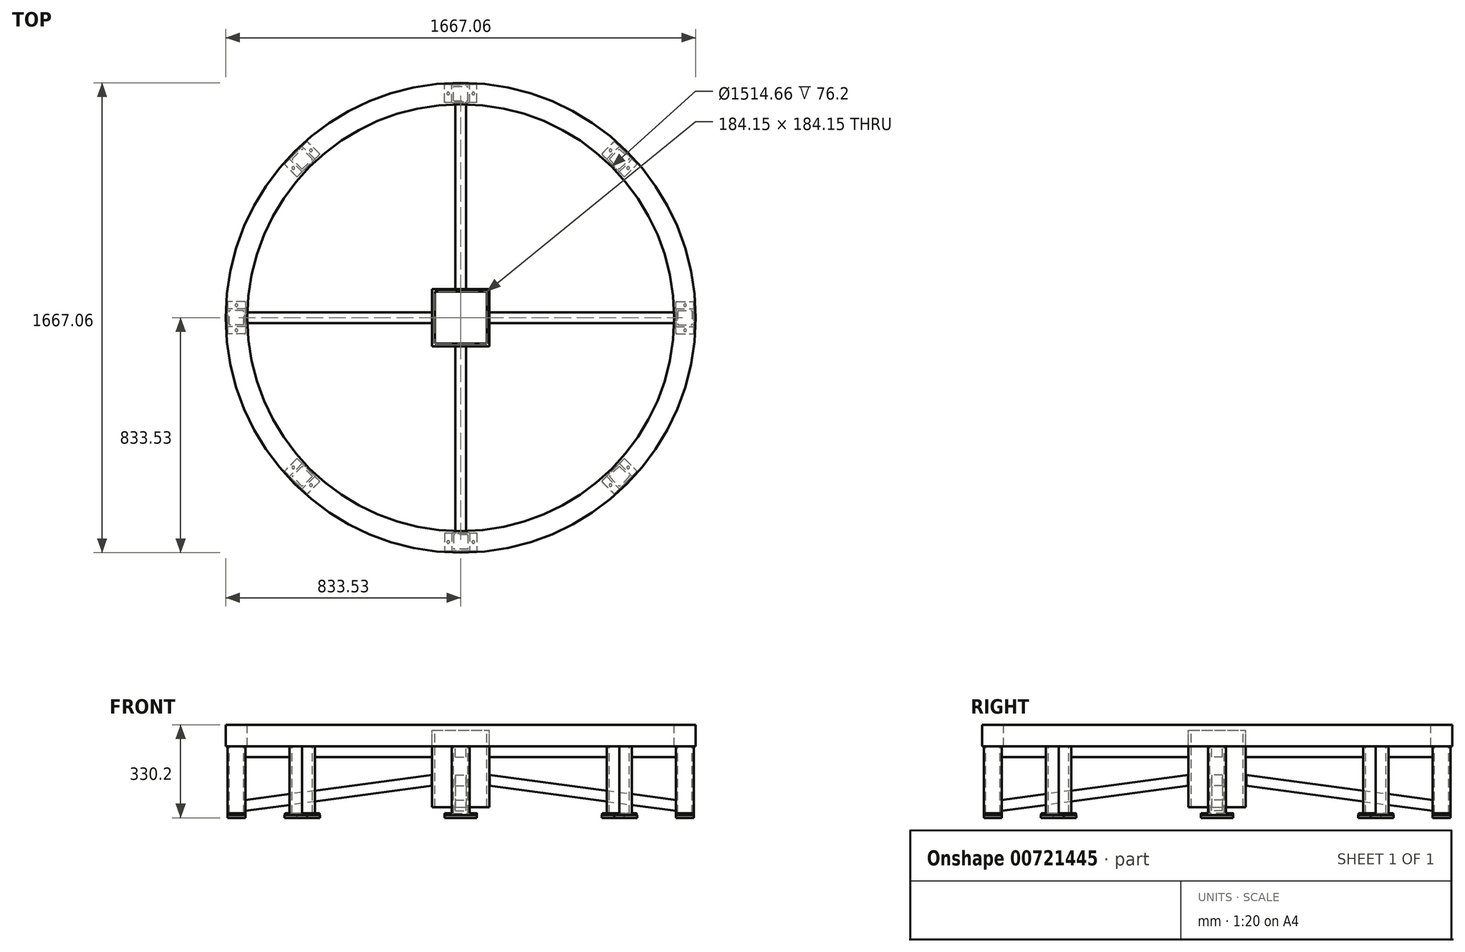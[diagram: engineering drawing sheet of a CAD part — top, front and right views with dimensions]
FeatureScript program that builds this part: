
annotation { "Feature Type Name" : "Feature", "Feature Type Description" : "" }
export const myFeature = defineFeature(function(context is Context, id is Id, definition is map)
    precondition{}
    {
        {
            var Q0;
            Q0=qCreatedBy(makeId("Front.planeOp"),FACE);
            var sketch = newSketch(context, id + "F0", { "sketchPlane" : qUnion([Q0])});
            skLineSegment(sketch, "E0.bottom", {"start": v(757.33, 0) * mm, "end": v(833.53, 0) * mm});
            skLineSegment(sketch, "E0.top", {"start": v(757.33, -76.2) * mm, "end": v(833.53, -76.2) * mm});
            skLineSegment(sketch, "E0.left", {"start": v(757.33, 0) * mm, "end": v(757.33, -76.2) * mm});
            skLineSegment(sketch, "E0.right", {"start": v(833.53, 0) * mm, "end": v(833.53, -76.2) * mm});
            skLineSegment(sketch, "E1.0", {"start": v(763.68, -69.85) * mm, "end": v(827.18, -69.85) * mm});
            skLineSegment(sketch, "E2.0", {"start": v(763.68, -6.35) * mm, "end": v(763.68, -69.85) * mm});
            skLineSegment(sketch, "E3.0", {"start": v(763.68, -6.35) * mm, "end": v(827.18, -6.35) * mm});
            skLineSegment(sketch, "E4.0", {"start": v(827.18, -6.35) * mm, "end": v(827.18, -69.85) * mm});
            skLineSegment(sketch, "E5", {"start": v(0, 0) * mm, "end": v(0, -46.56) * mm, "construction": true});
            skSolve(sketch);
        }
        {
            var Q0;
            Q0=makeQuery(id+"F0.imprint","IMPRINT",FACE,{"disambiguationData":[TD([[makeQuery(id+"F0.imprint","IMPRINT",EDGE,{"derivedFrom":sQuery(id+"F0.wireOp",EDGE,"E0.bottom")}),-1.0]])]});
            var Q1;
            Q1=makeQuery(id+"F0.imprint","IMPRINT",FACE,{"disambiguationData":[TD([[makeQuery(id+"F0.imprint","IMPRINT",EDGE,{"derivedFrom":sQuery(id+"F0.wireOp",EDGE,"E1.0")}),1.0]])]});
            var Q2;
            Q2=sQuery(id+"F0.wireOp",EDGE,"E0.bottom");
            var Q3;
            Q3=sQuery(id+"F0.wireOp",EDGE,"E3.0");
            var Q4;
            Q4=sQuery(id+"F0.wireOp",EDGE,"E0.left");
            var Q5;
            Q5=sQuery(id+"F0.wireOp",EDGE,"E1.0");
            var Q6;
            Q6=sQuery(id+"F0.wireOp",EDGE,"E0.top");
            var Q7;
            Q7=sQuery(id+"F0.wireOp",EDGE,"E4.0");
            var Q8;
            Q8=sQuery(id+"F0.wireOp",EDGE,"E0.right");
            var Q9;
            Q9=sQuery(id+"F0.wireOp",EDGE,"E2.0");
            var Q10;
            Q10=sQuery(id+"F0.wireOp",EDGE,"E5");
            revolve(context, id + "F1", {"surfaceOperationType" : NewSurfaceOperationType.NEW, "entities" : qUnion([Q0, Q1]), "surfaceEntities" : qUnion([Q2, Q3, Q4, Q5, Q6, Q7, Q8, Q9]), "axis" : qUnion([Q10]), "revolveType" : RevolveType.FULL});
        }
        {
            var Q0;
            Q0=qCreatedBy(makeId("Top.planeOp"),FACE);
            cPlane(context, id + "F2", {"entities" : qUnion([Q0]), "cplaneType" : CPlaneType.OFFSET, "offset" : 76.2 * mm, "oppositeDirection" : true, "width" : 152.4 * mm, "height" : 152.4 * mm});
        }
        {
            var Q0;
            Q0=qCreatedBy(id+"F2.planeOp",FACE);
            var sketch = newSketch(context, id + "F3", { "sketchPlane" : qUnion([Q0])});
            skLineSegment(sketch, "E6.bottom", {"start": v(-31.75, 763.68) * mm, "end": v(31.75, 763.68) * mm});
            skLineSegment(sketch, "E6.top", {"start": v(-31.75, 827.18) * mm, "end": v(31.75, 827.18) * mm});
            skLineSegment(sketch, "E6.left", {"start": v(-31.75, 763.68) * mm, "end": v(-31.75, 827.18) * mm});
            skLineSegment(sketch, "E6.right", {"start": v(31.75, 763.68) * mm, "end": v(31.75, 827.18) * mm});
            skLineSegment(sketch, "E7.0", {"start": v(-25.4, 770.03) * mm, "end": v(25.4, 770.03) * mm});
            skLineSegment(sketch, "E8.0", {"start": v(-25.4, 770.03) * mm, "end": v(-25.4, 820.83) * mm});
            skLineSegment(sketch, "E9.0", {"start": v(-25.4, 820.83) * mm, "end": v(25.4, 820.83) * mm});
            skLineSegment(sketch, "E10.0", {"start": v(25.4, 770.03) * mm, "end": v(25.4, 820.83) * mm});
            skSolve(sketch);
        }
        {
            var Q0;
            Q0=qSketchRegion(id+"F3",true);
            extrude(context, id + "F4", {"entities" : qUnion([Q0]), "oppositeDirection" : true, "depth" : 238.12 * mm, "offsetDistance" : 25.4 * mm});
        }
        {
            var Q0;
            Q0=makeQuery(id+"F4.opExtrude","CAP_FACE",FACE,{"disambiguationData":[OSD([sQuery(id+"F3.wireOp",EDGE,"E6.bottom"),sQuery(id+"F3.wireOp",EDGE,"E6.top"),sQuery(id+"F3.wireOp",EDGE,"E6.left"),sQuery(id+"F3.wireOp",EDGE,"E6.right"),sQuery(id+"F3.wireOp",EDGE,"E7.0"),sQuery(id+"F3.wireOp",EDGE,"E8.0"),sQuery(id+"F3.wireOp",EDGE,"E9.0"),sQuery(id+"F3.wireOp",EDGE,"E10.0")])],"isStart":false});
            var sketch = newSketch(context, id + "F5", { "sketchPlane" : qUnion([Q0])});
            skLineSegment(sketch, "E11.bottom", {"start": v(57.15, -763.68) * mm, "end": v(-57.15, -763.68) * mm});
            skLineSegment(sketch, "E11.top", {"start": v(57.15, -827.18) * mm, "end": v(-57.15, -827.18) * mm});
            skLineSegment(sketch, "E11.left", {"start": v(57.15, -763.68) * mm, "end": v(57.15, -827.18) * mm});
            skLineSegment(sketch, "E11.right", {"start": v(-57.15, -763.68) * mm, "end": v(-57.15, -827.18) * mm});
            skCircle(sketch, "E12", {"center": v(44.45, -795.43) * mm, "radius": 4.76 * mm});
            skCircle(sketch, "E13.1.0.0", {"center": v(-44.45, -795.43) * mm, "radius": 4.76 * mm});
            skLineSegment(sketch, "E13.direction1", {"start": v(44.45, -795.43) * mm, "end": v(-44.45, -795.43) * mm, "construction": true});
            skSolve(sketch);
        }
        {
            var Q0;
            Q0 = qSketchRegion(id + "F5", true);
            extrude(context, id + "F6", {"entities" : qUnion([Q0]), "operationType" : NewBodyOperationType.ADD, "depth" : 6.35 * mm, "offsetDistance" : 25.4 * mm});
        }
        {
            var Q0;
            Q0=makeQuery(id+"F6.opExtrude","SWEPT_EDGE",EDGE,{"disambiguationData":[OSD([sQuery(id+"F5.wireOp",EDGE,"E11.top"),sQuery(id+"F5.wireOp",EDGE,"E11.left")])]});
            var Q1;
            Q1=makeQuery(id+"F6.opExtrude","SWEPT_EDGE",EDGE,{"disambiguationData":[OSD([sQuery(id+"F5.wireOp",EDGE,"E11.bottom"),sQuery(id+"F5.wireOp",EDGE,"E11.left")])]});
            var Q2;
            Q2=makeQuery(id+"F6.opExtrude","SWEPT_EDGE",EDGE,{"disambiguationData":[OSD([sQuery(id+"F5.wireOp",EDGE,"E11.top"),sQuery(id+"F5.wireOp",EDGE,"E11.right")])]});
            var Q3;
            Q3=makeQuery(id+"F6.opExtrude","SWEPT_EDGE",EDGE,{"disambiguationData":[OSD([sQuery(id+"F5.wireOp",EDGE,"E11.bottom"),sQuery(id+"F5.wireOp",EDGE,"E11.right")])]});
            fillet(context, id + "F7", {"entities" : qUnion([Q0, Q1, Q2, Q3]), "radius" : 3.17 * mm, "tangentPropagation" : true, "allowEdgeOverflow" : false});
        }
        {
            var Q0;
            Q0=makeQuery(id+"F6.opExtrude","CAP_FACE",FACE,{"disambiguationData":[OSD([sQuery(id+"F5.wireOp",EDGE,"E11.bottom"),sQuery(id+"F5.wireOp",EDGE,"E11.top"),sQuery(id+"F5.wireOp",EDGE,"E11.left"),sQuery(id+"F5.wireOp",EDGE,"E11.right"),sQuery(id+"F5.wireOp",EDGE,"E12"),sQuery(id+"F5.wireOp",EDGE,"E13.1.0.0")])],"isStart":false});
            var sketch = newSketch(context, id + "F8", { "sketchPlane" : qUnion([Q0])});
            skLineSegment(sketch, "E14.bottom", {"start": v(57.15, -763.68) * mm, "end": v(-57.15, -763.68) * mm});
            skLineSegment(sketch, "E14.top", {"start": v(57.15, -827.18) * mm, "end": v(-57.15, -827.18) * mm});
            skLineSegment(sketch, "E14.left", {"start": v(57.15, -763.68) * mm, "end": v(57.15, -827.18) * mm});
            skLineSegment(sketch, "E14.right", {"start": v(-57.15, -763.68) * mm, "end": v(-57.15, -827.18) * mm});
            skSolve(sketch);
        }
        {
            var Q0;
            Q0 = qSketchRegion(id + "F8", true);
            extrude(context, id + "F9", {"entities" : qUnion([Q0]), "depth" : 9.52 * mm, "offsetDistance" : 25.4 * mm});
        }
        {
            var Q0;
            Q0=makeQuery(id+"F4.opExtrude","SWEPT_BODY",BODY,{"disambiguationData":[OSD([sQuery(id+"F3.wireOp",EDGE,"E6.bottom"),sQuery(id+"F3.wireOp",EDGE,"E6.top"),sQuery(id+"F3.wireOp",EDGE,"E6.left"),sQuery(id+"F3.wireOp",EDGE,"E6.right"),sQuery(id+"F3.wireOp",EDGE,"E7.0"),sQuery(id+"F3.wireOp",EDGE,"E8.0"),sQuery(id+"F3.wireOp",EDGE,"E9.0"),sQuery(id+"F3.wireOp",EDGE,"E10.0")])]});
            var Q1;
            Q1=makeQuery(id+"F9.opExtrude","SWEPT_BODY",BODY,{"disambiguationData":[OSD([sQuery(id+"F8.wireOp",EDGE,"E14.bottom"),sQuery(id+"F8.wireOp",EDGE,"E14.top"),sQuery(id+"F8.wireOp",EDGE,"E14.left"),sQuery(id+"F8.wireOp",EDGE,"E14.right")])]});
            var Q2;
            Q2=makeQuery(id+"F1.opRevolve","SWEPT_EDGE",EDGE,{"disambiguationData":[OSD([sQuery(id+"F0.wireOp",EDGE,"E0.bottom"),sQuery(id+"F0.wireOp",EDGE,"E0.left")])]});
            circularPattern(context, id + "F10", {"entities" : qUnion([Q0, Q1]), "axis" : qUnion([Q2]), "angle" : 360 * degree, "instanceCount" : 8, "equalSpace" : true});
        }
        {
            var Q0;
            Q0=qCreatedBy(id+"F2.planeOp",FACE);
            var sketch = newSketch(context, id + "F11", { "sketchPlane" : qUnion([Q0])});
            skLineSegment(sketch, "E15.bottom", {"start": v(-101.6, -101.6) * mm, "end": v(101.6, -101.6) * mm});
            skLineSegment(sketch, "E15.top", {"start": v(-101.6, 101.6) * mm, "end": v(101.6, 101.6) * mm});
            skLineSegment(sketch, "E15.left", {"start": v(-101.6, -101.6) * mm, "end": v(-101.6, 101.6) * mm});
            skLineSegment(sketch, "E15.right", {"start": v(101.6, -101.6) * mm, "end": v(101.6, 101.6) * mm});
            skLineSegment(sketch, "E16.0", {"start": v(-92.07, -92.08) * mm, "end": v(-92.08, 92.08) * mm});
            skLineSegment(sketch, "E16.1", {"start": v(-92.07, -92.08) * mm, "end": v(92.08, -92.08) * mm});
            skLineSegment(sketch, "E16.2", {"start": v(92.08, -92.08) * mm, "end": v(92.07, 92.07) * mm});
            skLineSegment(sketch, "E16.3", {"start": v(-92.08, 92.08) * mm, "end": v(92.07, 92.08) * mm});
            skSolve(sketch);
        }
        {
            var Q0;
            Q0=qSketchRegion(id+"F11",true);
            extrude(context, id + "F12", {"entities" : qUnion([Q0]), "oppositeDirection" : true, "depth" : 215.9 * mm, "offsetDistance" : 25.4 * mm, "hasSecondDirection" : true, "secondDirectionOppositeDirection" : false, "secondDirectionDepth" : 56.64 * mm});
        }
        {
            var Q0;
            Q0=qCreatedBy(id+"F2.planeOp",FACE);
            var sketch = newSketch(context, id + "F13", { "sketchPlane" : qUnion([Q0])});
            skLineSegment(sketch, "E17", {"start": v(0, 0) * mm, "end": v(781.72, 0) * mm, "construction": true});
            skLineSegment(sketch, "E18.0", {"start": v(101.6, -19.05) * mm, "end": v(763.68, -19.05) * mm});
            skLineSegment(sketch, "E19.0", {"start": v(101.6, 19.05) * mm, "end": v(763.68, 19.05) * mm});
            skLineSegment(sketch, "E20", {"start": v(0, 0) * mm, "end": v(0, -19.05) * mm});
            skLineSegment(sketch, "E21.0", {"start": v(101.6, 19.05) * mm, "end": v(101.6, -19.05) * mm});
            skLineSegment(sketch, "E22.0", {"start": v(763.68, 19.05) * mm, "end": v(763.68, -19.05) * mm});
            skLineSegment(sketch, "E23.1.0", {"start": v(19.05, 101.6) * mm, "end": v(19.05, 763.68) * mm});
            skLineSegment(sketch, "E23.1.1", {"start": v(-19.05, 101.6) * mm, "end": v(-19.05, 763.68) * mm});
            skLineSegment(sketch, "E23.1.2", {"start": v(-19.05, 101.6) * mm, "end": v(19.05, 101.6) * mm});
            skLineSegment(sketch, "E23.1.3", {"start": v(-19.05, 763.68) * mm, "end": v(19.05, 763.68) * mm});
            skLineSegment(sketch, "E23.2.0", {"start": v(-101.6, 19.05) * mm, "end": v(-763.68, 19.05) * mm});
            skLineSegment(sketch, "E23.2.1", {"start": v(-101.6, -19.05) * mm, "end": v(-763.68, -19.05) * mm});
            skLineSegment(sketch, "E23.2.2", {"start": v(-101.6, -19.05) * mm, "end": v(-101.6, 19.05) * mm});
            skLineSegment(sketch, "E23.2.3", {"start": v(-763.68, -19.05) * mm, "end": v(-763.68, 19.05) * mm});
            skLineSegment(sketch, "E23.3.0", {"start": v(-19.05, -101.6) * mm, "end": v(-19.05, -763.68) * mm});
            skLineSegment(sketch, "E23.3.1", {"start": v(19.05, -101.6) * mm, "end": v(19.05, -763.68) * mm});
            skLineSegment(sketch, "E23.3.2", {"start": v(19.05, -101.6) * mm, "end": v(-19.05, -101.6) * mm});
            skLineSegment(sketch, "E23.3.3", {"start": v(19.05, -763.68) * mm, "end": v(-19.05, -763.68) * mm});
            skPoint(sketch, "E23.center", {"position": v(0, 0) * mm});
            skSolve(sketch);
        }
        {
            var Q0;
            Q0=qSketchRegion(id+"F13",true);
            extrude(context, id + "F14", {"entities" : qUnion([Q0]), "oppositeDirection" : true, "depth" : 38.1 * mm, "offsetDistance" : 25.4 * mm});
        }
        {
            var Q0;
            Q0=qCreatedBy(makeId("Right.planeOp"),FACE);
            var sketch = newSketch(context, id + "F15", { "sketchPlane" : qUnion([Q0])});
            skLineSegment(sketch, "E24.0", {"start": v(-103.35, -216.25) * mm, "end": v(-765.43, -305.9) * mm});
            skLineSegment(sketch, "E25.0", {"start": v(-103.35, -177.8) * mm, "end": v(-765.43, -267.46) * mm});
            skLineSegment(sketch, "E26", {"start": v(-103.35, -216.25) * mm, "end": v(-103.35, -177.8) * mm});
            skLineSegment(sketch, "E27.0", {"start": v(-765.43, -305.9) * mm, "end": v(-765.43, -267.46) * mm});
            skSolve(sketch);
        }
        {
            var Q0;
            Q0=qSketchRegion(id+"F15",true);
            extrude(context, id + "F16", {"entities" : qUnion([Q0]), "depth" : 19.05 * mm, "offsetDistance" : 25.4 * mm, "hasSecondDirection" : true, "secondDirectionOppositeDirection" : true, "secondDirectionDepth" : 19.05 * mm});
        }
        {
            var Q0;
            Q0=makeQuery(id+"F16.opExtrude","SWEPT_BODY",BODY,{"disambiguationData":[OSD([sQuery(id+"F15.wireOp",EDGE,"E24.0"),sQuery(id+"F15.wireOp",EDGE,"E25.0"),sQuery(id+"F15.wireOp",EDGE,"E26"),sQuery(id+"F15.wireOp",EDGE,"E27.0")])]});
            var Q1;
            Q1=makeQuery(id+"F1.opRevolve","SWEPT_EDGE",EDGE,{"disambiguationData":[OSD([sQuery(id+"F0.wireOp",EDGE,"E0.top"),sQuery(id+"F0.wireOp",EDGE,"E0.right")])]});
            circularPattern(context, id + "F17", {"entities" : qUnion([Q0]), "axis" : qUnion([Q1]), "angle" : 360 * degree, "instanceCount" : 4, "equalSpace" : true});
        }
    });
